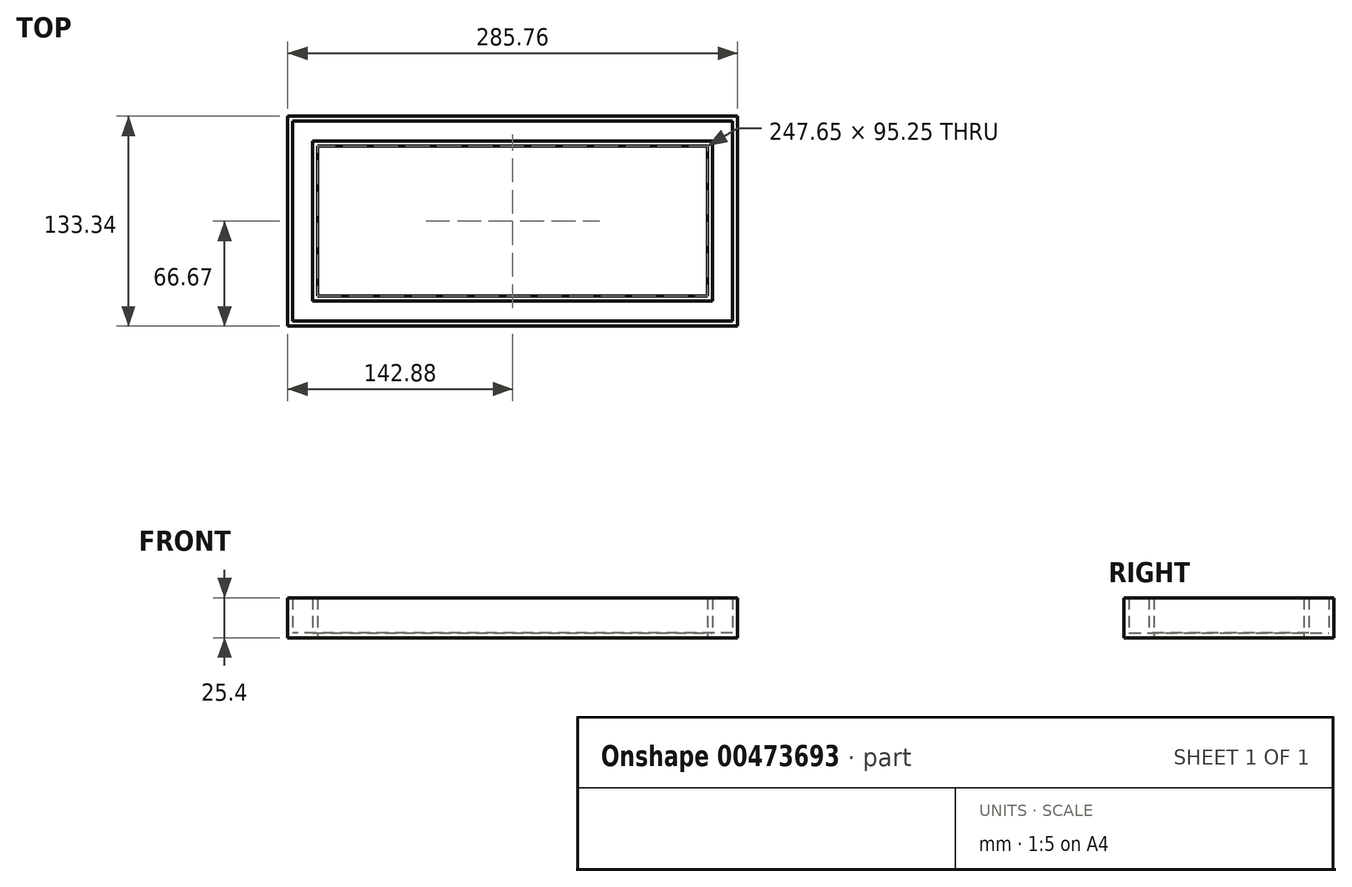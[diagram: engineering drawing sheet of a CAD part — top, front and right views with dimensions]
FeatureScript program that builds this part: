
annotation { "Feature Type Name" : "Feature", "Feature Type Description" : "" }
export const myFeature = defineFeature(function(context is Context, id is Id, definition is map)
    precondition{}
    {
        {
            var Q0;
            Q0=qCreatedBy(makeId("Top.planeOp"),FACE);
            var sketch = newSketch(context, id + "F0", { "sketchPlane" : qUnion([Q0])});
            skLineSegment(sketch, "E0.bottom", {"start": v(-139.7, -63.5) * mm, "end": v(139.7, -63.5) * mm});
            skLineSegment(sketch, "E0.top", {"start": v(-139.7, 63.5) * mm, "end": v(139.7, 63.5) * mm});
            skLineSegment(sketch, "E0.left", {"start": v(-139.7, -63.5) * mm, "end": v(-139.7, 63.5) * mm});
            skLineSegment(sketch, "E0.right", {"start": v(139.7, -63.5) * mm, "end": v(139.7, 63.5) * mm});
            skSolve(sketch);
        }
        {
            var Q0;
            Q0=qCreatedBy(makeId("Top.planeOp"),FACE);
            var sketch = newSketch(context, id + "F1", { "sketchPlane" : qUnion([Q0])});
            skLineSegment(sketch, "E1.bottom", {"start": v(-127, 50.8) * mm, "end": v(127, 50.8) * mm});
            skLineSegment(sketch, "E1.top", {"start": v(-127, -50.8) * mm, "end": v(127, -50.8) * mm});
            skLineSegment(sketch, "E1.left", {"start": v(-127, 50.8) * mm, "end": v(-127, -50.8) * mm});
            skLineSegment(sketch, "E1.right", {"start": v(127, 50.8) * mm, "end": v(127, -50.8) * mm});
            skLineSegment(sketch, "E2.0.0", {"start": v(139.7, 63.5) * mm, "end": v(-139.7, 63.5) * mm});
            skLineSegment(sketch, "E2.0.1", {"start": v(-139.7, 63.5) * mm, "end": v(-139.7, -63.5) * mm});
            skLineSegment(sketch, "E2.0.2", {"start": v(-139.7, -63.5) * mm, "end": v(139.7, -63.5) * mm});
            skLineSegment(sketch, "E2.0.3", {"start": v(139.7, -63.5) * mm, "end": v(139.7, 63.5) * mm});
            skSolve(sketch);
        }
        {
            var Q0;
            Q0=makeQuery(id+"F0.imprint","IMPRINT",FACE,{"disambiguationData":[TD([[makeQuery(id+"F0.imprint","IMPRINT",EDGE,{"derivedFrom":sQuery(id+"F0.wireOp",EDGE,"E0.bottom")}),1.0]])]});
            var sketch = newSketch(context, id + "F2", { "sketchPlane" : qUnion([Q0])});
            skLineSegment(sketch, "E3.bottom", {"start": v(-142.87, 66.68) * mm, "end": v(142.88, 66.68) * mm});
            skLineSegment(sketch, "E3.top", {"start": v(-142.87, -66.67) * mm, "end": v(142.88, -66.67) * mm});
            skLineSegment(sketch, "E3.left", {"start": v(-142.87, 66.67) * mm, "end": v(-142.87, -66.67) * mm});
            skLineSegment(sketch, "E3.right", {"start": v(142.88, 66.67) * mm, "end": v(142.88, -66.67) * mm});
            skSolve(sketch);
        }
        {
            var Q0;
            Q0=makeQuery(id+"F1.imprint","IMPRINT",FACE,{"disambiguationData":[TD([[makeQuery(id+"F1.imprint","IMPRINT",EDGE,{"derivedFrom":sQuery(id+"F1.wireOp",EDGE,"E1.bottom")}),1.0]])]});
            extrude(context, id + "F3", {"entities" : qUnion([Q0]), "depth" : 3.17 * mm});
        }
        {
            var Q0;
            Q0=makeQuery(id+"F2.imprint","IMPRINT",FACE,{"disambiguationData":[TD([[makeQuery(id+"F2.imprint","IMPRINT",EDGE,{"derivedFrom":makeQuery(id+"F0.imprint","IMPRINT",EDGE,{"derivedFrom":sQuery(id+"F0.wireOp",EDGE,"E0.bottom")})}),1.0]])]});
            var sketch = newSketch(context, id + "F4", { "sketchPlane" : qUnion([Q0])});
            skLineSegment(sketch, "E4", {"start": v(0, -64.32) * mm, "end": v(0, 64.68) * mm, "construction": true});
            skSolve(sketch);
        }
        {
            var Q0;
            Q0=makeQuery(id+"F2.imprint","IMPRINT",FACE,{"disambiguationData":[TD([[makeQuery(id+"F2.imprint","IMPRINT",EDGE,{"derivedFrom":makeQuery(id+"F0.imprint","IMPRINT",EDGE,{"derivedFrom":sQuery(id+"F0.wireOp",EDGE,"E0.bottom")})}),1.0]])]});
            var sketch = newSketch(context, id + "F5", { "sketchPlane" : qUnion([Q0])});
            skLineSegment(sketch, "E5.bottom", {"start": v(-123.82, 47.63) * mm, "end": v(123.83, 47.63) * mm});
            skLineSegment(sketch, "E5.top", {"start": v(-123.82, -47.62) * mm, "end": v(123.83, -47.62) * mm});
            skLineSegment(sketch, "E5.left", {"start": v(-123.82, 47.63) * mm, "end": v(-123.82, -47.62) * mm});
            skLineSegment(sketch, "E5.right", {"start": v(123.83, 47.63) * mm, "end": v(123.83, -47.62) * mm});
            skSolve(sketch);
        }
        {
            var Q0;
            Q0=makeQuery(id+"F2.imprint","IMPRINT",FACE,{"disambiguationData":[TD([[makeQuery(id+"F2.imprint","IMPRINT",EDGE,{"derivedFrom":sQuery(id+"F2.wireOp",EDGE,"E3.bottom")}),-1.0]])]});
            extrude(context, id + "F6", {"entities" : qUnion([Q0]), "operationType" : NewBodyOperationType.ADD, "depth" : 25.4 * mm});
        }
        {
            var Q0;
            Q0=makeQuery(id+"F4.imprint","IMPRINT",FACE,{"disambiguationData":[TD([[makeQuery(id+"F4.imprint","IMPRINT",EDGE,{"derivedFrom":makeQuery(id+"F2.imprint","IMPRINT",EDGE,{"derivedFrom":makeQuery(id+"F0.imprint","IMPRINT",EDGE,{"derivedFrom":sQuery(id+"F0.wireOp",EDGE,"E0.bottom")})})}),1.0]])]});
            var sketch = newSketch(context, id + "F7", { "sketchPlane" : qUnion([Q0])});
            skLineSegment(sketch, "E6.0", {"start": v(-123.82, 47.63) * mm, "end": v(123.83, 47.63) * mm});
            skLineSegment(sketch, "E7.0", {"start": v(-123.82, 47.63) * mm, "end": v(-123.82, -47.62) * mm});
            skLineSegment(sketch, "E8.0", {"start": v(-123.82, -47.62) * mm, "end": v(123.83, -47.62) * mm});
            skLineSegment(sketch, "E9.0", {"start": v(123.83, 47.63) * mm, "end": v(123.83, -47.62) * mm});
            skLineSegment(sketch, "E10.0", {"start": v(127, 50.8) * mm, "end": v(127, -50.8) * mm});
            skLineSegment(sketch, "E11.0", {"start": v(-127, -50.8) * mm, "end": v(127, -50.8) * mm});
            skLineSegment(sketch, "E12.0", {"start": v(-127, 50.8) * mm, "end": v(-127, -50.8) * mm});
            skLineSegment(sketch, "E13.0", {"start": v(-127, 50.8) * mm, "end": v(127, 50.8) * mm});
            skSolve(sketch);
        }
        {
            var Q0;
            Q0 = qSketchRegion(id + "F7", true);
            extrude(context, id + "F8", {"entities" : qUnion([Q0]), "operationType" : NewBodyOperationType.ADD, "depth" : 25.4 * mm});
        }
    });
